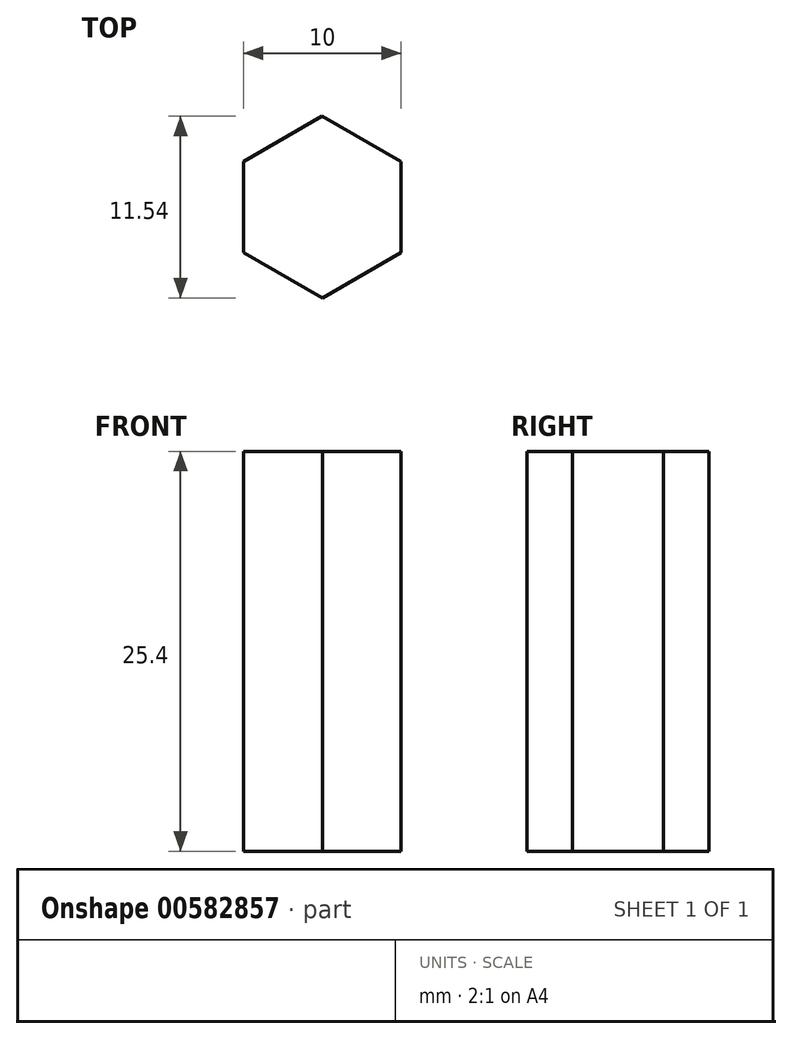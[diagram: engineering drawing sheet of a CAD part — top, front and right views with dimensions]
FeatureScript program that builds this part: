
annotation { "Feature Type Name" : "Feature", "Feature Type Description" : "" }
export const myFeature = defineFeature(function(context is Context, id is Id, definition is map)
    precondition{}
    {
        {
            var Q0;
            Q0=qCreatedBy(makeId("Top.planeOp"),FACE);
            var sketch = newSketch(context, id + "F0", { "sketchPlane" : qUnion([Q0])});
            skCircle(sketch, "E0.cCircle", {"center": v(0, 0) * mm, "radius": 5 * mm, "construction": true});
            skLineSegment(sketch, "E0.0", {"start": v(0, 5.77) * mm, "end": v(5, 2.9) * mm});
            skLineSegment(sketch, "E0.1", {"start": v(5, 2.9) * mm, "end": v(5, -2.88) * mm});
            skLineSegment(sketch, "E0.2", {"start": v(5, -2.88) * mm, "end": v(0, -5.77) * mm});
            skLineSegment(sketch, "E0.3", {"start": v(0, -5.77) * mm, "end": v(-5, -2.9) * mm});
            skLineSegment(sketch, "E0.4", {"start": v(-5, -2.9) * mm, "end": v(-5, 2.88) * mm});
            skLineSegment(sketch, "E0.5", {"start": v(-5, 2.88) * mm, "end": v(0, 5.77) * mm});
            skPoint(sketch, "E0.0.midPoint", {"position": v(2.5, 4.33) * mm});
            skSolve(sketch);
        }
        {
            var Q0;
            Q0=makeQuery(id+"F0.imprint","IMPRINT",FACE,{"disambiguationData":[TD([[makeQuery(id+"F0.imprint","IMPRINT",EDGE,{"derivedFrom":sQuery(id+"F0.wireOp",EDGE,"E0.0")}),-1.0]])]});
            extrude(context, id + "F1", {"entities" : qUnion([Q0]), "depth" : 25.4 * mm, "offsetDistance" : 25.4 * mm});
        }
    });
